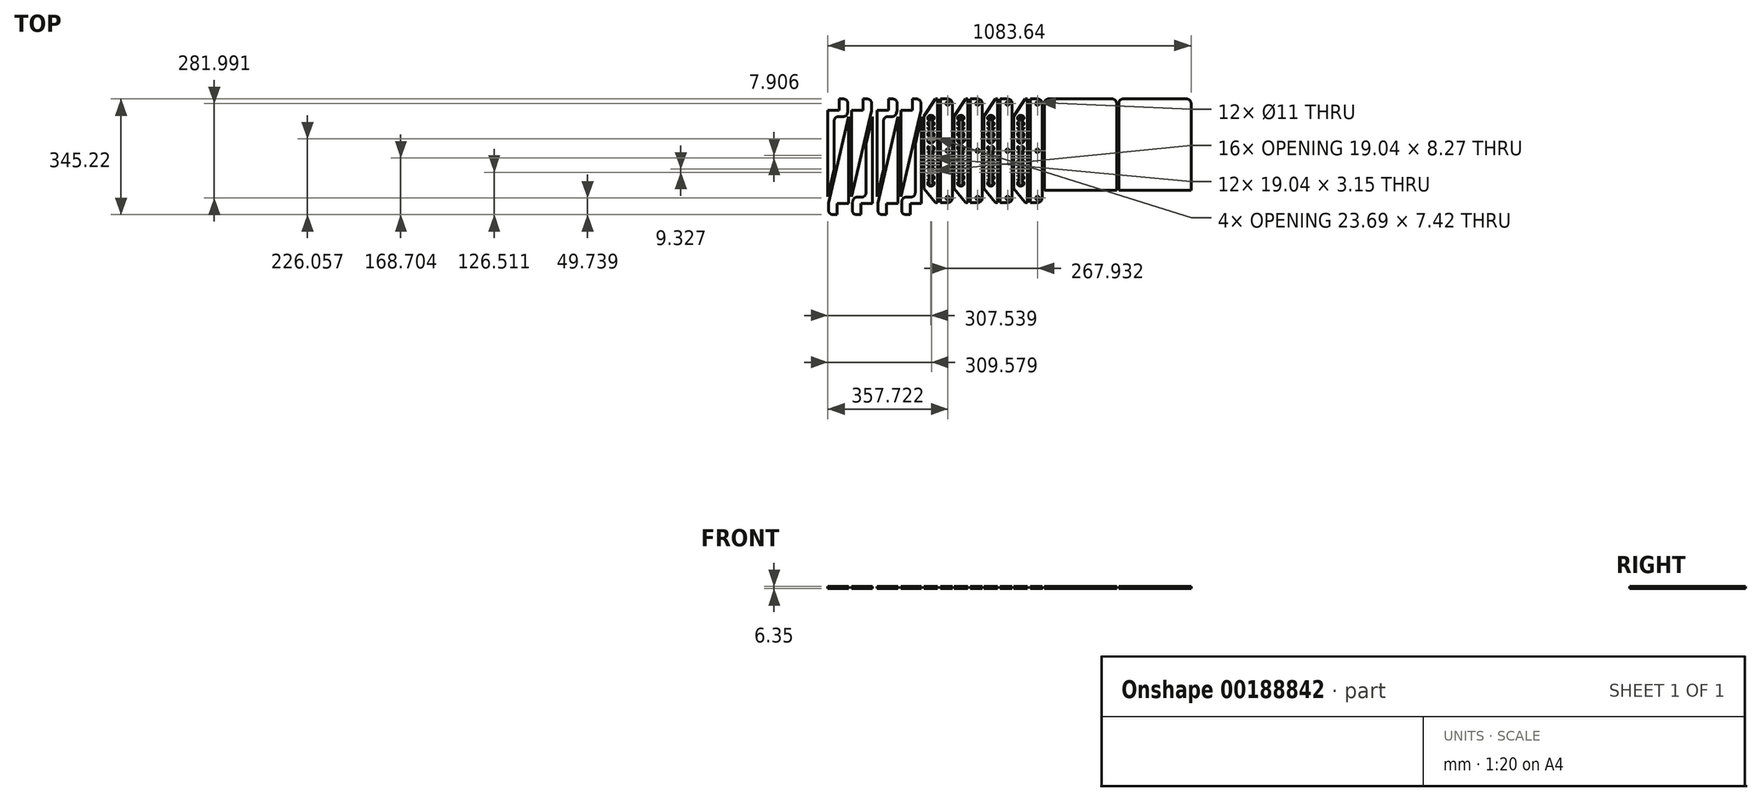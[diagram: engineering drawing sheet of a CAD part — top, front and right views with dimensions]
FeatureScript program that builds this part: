
annotation { "Feature Type Name" : "Feature", "Feature Type Description" : "" }
export const myFeature = defineFeature(function(context is Context, id is Id, definition is map)
    precondition{}
    {
        {
            var Q0;
            Q0=qCreatedBy(makeId("Top.planeOp"),FACE);
            var sketch = newSketch(context, id + "F0", { "sketchPlane" : qUnion([Q0])});
            skLineSegment(sketch, "E0.bottom", {"start": v(-174.96, 148.75) * mm, "end": v(40.94, 148.75) * mm});
            skLineSegment(sketch, "E0.top", {"start": v(-162.26, 421.8) * mm, "end": v(28.24, 421.8) * mm});
            skLineSegment(sketch, "E0.left", {"start": v(-174.96, 148.75) * mm, "end": v(-174.96, 409.1) * mm});
            skLineSegment(sketch, "E0.right", {"start": v(40.94, 148.75) * mm, "end": v(40.94, 409.1) * mm});
            skPoint(sketch, "E1.visualSharp", {"position": v(-174.96, 421.8) * mm});
            skArc(sketch, "E1.filletArc", {"start": v(-162.26, 421.8) * mm, "mid": v(-171.24, 418.08) * mm, "end": v(-174.96, 409.1) * mm});
            skPoint(sketch, "E2.visualSharp", {"position": v(40.94, 421.8) * mm});
            skArc(sketch, "E2.filletArc", {"start": v(40.94, 409.1) * mm, "mid": v(37.22, 418.08) * mm, "end": v(28.24, 421.8) * mm});
            skPoint(sketch, "E3", {"position": v(-194.8, 408.31) * mm});
            skPoint(sketch, "E4", {"position": v(-194.8, 267.31) * mm});
            skPoint(sketch, "E5", {"position": v(-194.8, 126.32) * mm});
            skLineSegment(sketch, "E6", {"start": v(-181.3, 125.53) * mm, "end": v(-181.3, 409.1) * mm});
            skLineSegment(sketch, "E7", {"start": v(-194, 112.83) * mm, "end": v(-216.87, 112.83) * mm});
            skLineSegment(sketch, "E8", {"start": v(-194, 421.8) * mm, "end": v(-216.87, 421.8) * mm});
            skPoint(sketch, "E9.visualSharp", {"position": v(-181.3, 112.83) * mm});
            skArc(sketch, "E9.filletArc", {"start": v(-194, 112.83) * mm, "mid": v(-185.03, 116.55) * mm, "end": v(-181.3, 125.53) * mm});
            skPoint(sketch, "E10.visualSharp", {"position": v(-181.3, 421.8) * mm});
            skArc(sketch, "E10.filletArc", {"start": v(-181.3, 409.1) * mm, "mid": v(-185.03, 418.08) * mm, "end": v(-194, 421.8) * mm});
            skLineSegment(sketch, "E11", {"start": v(-216.87, 112.83) * mm, "end": v(-216.87, 421.8) * mm});
            skLineSegment(sketch, "E12", {"start": v(-265.3, 154.26) * mm, "end": v(-265.3, 370.21) * mm});
            skLineSegment(sketch, "E13", {"start": v(-265.3, 370.21) * mm, "end": v(-231.01, 421.8) * mm});
            skLineSegment(sketch, "E14", {"start": v(-231.01, 421.8) * mm, "end": v(-224.66, 421.8) * mm});
            skLineSegment(sketch, "E15", {"start": v(-224.66, 421.8) * mm, "end": v(-224.66, 112.83) * mm});
            skLineSegment(sketch, "E16", {"start": v(-224.66, 112.83) * mm, "end": v(-231.01, 112.83) * mm});
            skLineSegment(sketch, "E17", {"start": v(-231.01, 112.83) * mm, "end": v(-265.3, 154.26) * mm});
            skText(sketch, "E18", { "text": "CUMMINS QSK60", "fontName": "AllertaStencil-Regular.ttf"});
            skLineSegment(sketch, "E19", {"start": v(-749.65, 129.9) * mm, "end": v(-690.3, 387.04) * mm});
            skLineSegment(sketch, "E20", {"start": v(-689.96, 389.9) * mm, "end": v(-689.96, 409.1) * mm});
            skLineSegment(sketch, "E21", {"start": v(-702.66, 421.8) * mm, "end": v(-715.36, 421.8) * mm});
            skLineSegment(sketch, "E22", {"start": v(-715.36, 421.8) * mm, "end": v(-715.36, 388.45) * mm});
            skLineSegment(sketch, "E23", {"start": v(-715.36, 388.45) * mm, "end": v(-749.65, 388.45) * mm});
            skLineSegment(sketch, "E24", {"start": v(-749.65, 388.45) * mm, "end": v(-749.65, 129.9) * mm});
            skPoint(sketch, "E25.visualSharp", {"position": v(-689.96, 421.8) * mm});
            skArc(sketch, "E25.filletArc", {"start": v(-689.96, 409.1) * mm, "mid": v(-693.68, 418.08) * mm, "end": v(-702.66, 421.8) * mm});
            skLineSegment(sketch, "E26", {"start": v(-760.76, 385.28) * mm, "end": v(-760.76, 409.1) * mm});
            skLineSegment(sketch, "E27", {"start": v(-773.46, 421.8) * mm, "end": v(-786.16, 421.8) * mm});
            skLineSegment(sketch, "E28", {"start": v(-786.16, 421.8) * mm, "end": v(-786.16, 388.45) * mm});
            skLineSegment(sketch, "E29", {"start": v(-786.16, 388.45) * mm, "end": v(-820.45, 388.45) * mm});
            skLineSegment(sketch, "E30", {"start": v(-820.45, 388.45) * mm, "end": v(-820.45, 129.9) * mm});
            skPoint(sketch, "E31.visualSharp", {"position": v(-760.76, 421.8) * mm});
            skArc(sketch, "E31.filletArc", {"start": v(-760.76, 409.1) * mm, "mid": v(-764.48, 418.08) * mm, "end": v(-773.46, 421.8) * mm});
            skPoint(sketch, "E32.visualSharp", {"position": v(-760.76, 388.45) * mm});
            skArc(sketch, "E32.filletArc", {"start": v(-761.08, 382.42) * mm, "mid": v(-760.84, 383.84) * mm, "end": v(-760.76, 385.28) * mm});
            skPoint(sketch, "E33.visualSharp", {"position": v(-689.96, 388.45) * mm});
            skArc(sketch, "E33.filletArc", {"start": v(-690.3, 387.04) * mm, "mid": v(-690.05, 388.46) * mm, "end": v(-689.96, 389.9) * mm});
            skLineSegment(sketch, "E34", {"start": v(-801.4, 356.7) * mm, "end": v(-801.4, 213.86) * mm});
            skLineSegment(sketch, "E35", {"start": v(-788.7, 369.4) * mm, "end": v(-774.2, 369.4) * mm});
            skLineSegment(sketch, "E36", {"start": v(-820.45, 129.9) * mm, "end": v(-801.72, 211) * mm});
            skLineSegment(sketch, "E37", {"start": v(-761.82, 379.24) * mm, "end": v(-761.08, 382.42) * mm});
            skPoint(sketch, "E38.visualSharp", {"position": v(-801.4, 212.42) * mm});
            skArc(sketch, "E38.filletArc", {"start": v(-801.72, 211) * mm, "mid": v(-801.48, 212.43) * mm, "end": v(-801.4, 213.86) * mm});
            skPoint(sketch, "E39.visualSharp", {"position": v(-764.09, 369.4) * mm});
            skArc(sketch, "E39.filletArc", {"start": v(-774.2, 369.4) * mm, "mid": v(-766.29, 372.16) * mm, "end": v(-761.82, 379.24) * mm});
            skPoint(sketch, "E40.visualSharp", {"position": v(-801.4, 369.4) * mm});
            skArc(sketch, "E40.filletArc", {"start": v(-788.7, 369.4) * mm, "mid": v(-797.68, 365.68) * mm, "end": v(-801.4, 356.7) * mm});
            skCircle(sketch, "E41", {"center": v(-194.8, 126.32) * mm, "radius": 5.5 * mm});
            skCircle(sketch, "E42", {"center": v(-194.8, 267.31) * mm, "radius": 5.5 * mm});
            skCircle(sketch, "E43", {"center": v(-194.8, 408.31) * mm, "radius": 5.5 * mm});
            skLineSegment(sketch, "E44", {"start": v(-602.6, 129.9) * mm, "end": v(-543.23, 387.04) * mm});
            skLineSegment(sketch, "E45", {"start": v(-542.9, 389.9) * mm, "end": v(-542.9, 409.1) * mm});
            skLineSegment(sketch, "E46", {"start": v(-555.6, 421.8) * mm, "end": v(-568.3, 421.8) * mm});
            skLineSegment(sketch, "E47", {"start": v(-568.3, 421.8) * mm, "end": v(-568.3, 388.45) * mm});
            skLineSegment(sketch, "E48", {"start": v(-568.3, 388.45) * mm, "end": v(-602.6, 388.45) * mm});
            skLineSegment(sketch, "E49", {"start": v(-602.6, 388.45) * mm, "end": v(-602.6, 129.9) * mm});
            skPoint(sketch, "E50.visualSharp", {"position": v(-542.9, 421.8) * mm});
            skArc(sketch, "E50.filletArc", {"start": v(-542.9, 409.1) * mm, "mid": v(-546.63, 418.08) * mm, "end": v(-555.6, 421.8) * mm});
            skLineSegment(sketch, "E51", {"start": v(-613.7, 389.9) * mm, "end": v(-613.7, 409.1) * mm});
            skLineSegment(sketch, "E52", {"start": v(-626.4, 421.8) * mm, "end": v(-639.1, 421.8) * mm});
            skLineSegment(sketch, "E53", {"start": v(-639.1, 421.8) * mm, "end": v(-639.1, 388.45) * mm});
            skLineSegment(sketch, "E54", {"start": v(-639.1, 388.45) * mm, "end": v(-673.39, 388.45) * mm});
            skLineSegment(sketch, "E55", {"start": v(-673.39, 388.45) * mm, "end": v(-673.39, 129.9) * mm});
            skPoint(sketch, "E56.visualSharp", {"position": v(-613.7, 421.8) * mm});
            skArc(sketch, "E56.filletArc", {"start": v(-613.7, 409.1) * mm, "mid": v(-617.42, 418.08) * mm, "end": v(-626.4, 421.8) * mm});
            skPoint(sketch, "E57.visualSharp", {"position": v(-613.7, 388.45) * mm});
            skArc(sketch, "E57.filletArc", {"start": v(-614.03, 387.04) * mm, "mid": v(-613.78, 388.46) * mm, "end": v(-613.7, 389.9) * mm});
            skPoint(sketch, "E58.visualSharp", {"position": v(-542.9, 388.45) * mm});
            skArc(sketch, "E58.filletArc", {"start": v(-543.23, 387.04) * mm, "mid": v(-542.99, 388.46) * mm, "end": v(-542.9, 389.9) * mm});
            skLineSegment(sketch, "E59", {"start": v(-654.34, 356.7) * mm, "end": v(-654.34, 213.86) * mm});
            skLineSegment(sketch, "E60", {"start": v(-641.64, 369.4) * mm, "end": v(-628.2, 369.4) * mm});
            skLineSegment(sketch, "E61", {"start": v(-673.39, 129.9) * mm, "end": v(-654.67, 211) * mm});
            skLineSegment(sketch, "E62", {"start": v(-615.83, 379.24) * mm, "end": v(-614.03, 387.04) * mm});
            skPoint(sketch, "E63.visualSharp", {"position": v(-654.34, 212.42) * mm});
            skArc(sketch, "E63.filletArc", {"start": v(-654.67, 211) * mm, "mid": v(-654.42, 212.43) * mm, "end": v(-654.34, 213.86) * mm});
            skPoint(sketch, "E64.visualSharp", {"position": v(-618.1, 369.4) * mm});
            skArc(sketch, "E64.filletArc", {"start": v(-628.2, 369.4) * mm, "mid": v(-620.3, 372.16) * mm, "end": v(-615.83, 379.24) * mm});
            skPoint(sketch, "E65.visualSharp", {"position": v(-654.34, 369.4) * mm});
            skArc(sketch, "E65.filletArc", {"start": v(-641.64, 369.4) * mm, "mid": v(-650.62, 365.68) * mm, "end": v(-654.34, 356.7) * mm});
            skPoint(sketch, "E66", {"position": v(-284.04, 408.31) * mm});
            skPoint(sketch, "E67", {"position": v(-284.04, 267.31) * mm});
            skPoint(sketch, "E68", {"position": v(-284.04, 126.32) * mm});
            skLineSegment(sketch, "E69", {"start": v(-270.55, 125.53) * mm, "end": v(-270.55, 409.1) * mm});
            skLineSegment(sketch, "E70", {"start": v(-283.25, 112.83) * mm, "end": v(-306.1, 112.83) * mm});
            skLineSegment(sketch, "E71", {"start": v(-283.25, 421.8) * mm, "end": v(-306.1, 421.8) * mm});
            skPoint(sketch, "E72.visualSharp", {"position": v(-270.55, 112.83) * mm});
            skArc(sketch, "E72.filletArc", {"start": v(-283.25, 112.83) * mm, "mid": v(-274.27, 116.55) * mm, "end": v(-270.55, 125.53) * mm});
            skPoint(sketch, "E73.visualSharp", {"position": v(-270.55, 421.8) * mm});
            skArc(sketch, "E73.filletArc", {"start": v(-270.55, 409.1) * mm, "mid": v(-274.27, 418.08) * mm, "end": v(-283.25, 421.8) * mm});
            skLineSegment(sketch, "E74", {"start": v(-306.1, 112.83) * mm, "end": v(-306.1, 421.8) * mm});
            skLineSegment(sketch, "E75", {"start": v(-354.54, 154.26) * mm, "end": v(-354.54, 370.21) * mm});
            skLineSegment(sketch, "E76", {"start": v(-354.54, 370.21) * mm, "end": v(-320.25, 421.8) * mm});
            skLineSegment(sketch, "E77", {"start": v(-320.25, 421.8) * mm, "end": v(-313.9, 421.8) * mm});
            skLineSegment(sketch, "E78", {"start": v(-313.9, 421.8) * mm, "end": v(-313.9, 112.83) * mm});
            skLineSegment(sketch, "E79", {"start": v(-313.9, 112.83) * mm, "end": v(-320.25, 112.83) * mm});
            skLineSegment(sketch, "E80", {"start": v(-320.25, 112.83) * mm, "end": v(-354.54, 154.26) * mm});
            skText(sketch, "E81", { "text": "CUMMINS QSK60", "fontName": "AllertaStencil-Regular.ttf"});
            skCircle(sketch, "E82", {"center": v(-284.04, 126.32) * mm, "radius": 5.5 * mm});
            skCircle(sketch, "E83", {"center": v(-284.04, 267.31) * mm, "radius": 5.5 * mm});
            skCircle(sketch, "E84", {"center": v(-284.04, 408.31) * mm, "radius": 5.5 * mm});
            skPoint(sketch, "E85", {"position": v(-373.49, 408.31) * mm});
            skPoint(sketch, "E86", {"position": v(-373.49, 267.31) * mm});
            skPoint(sketch, "E87", {"position": v(-373.49, 126.32) * mm});
            skLineSegment(sketch, "E88", {"start": v(-360, 125.53) * mm, "end": v(-360, 409.1) * mm});
            skLineSegment(sketch, "E89", {"start": v(-372.7, 112.83) * mm, "end": v(-395.56, 112.83) * mm});
            skLineSegment(sketch, "E90", {"start": v(-372.7, 421.8) * mm, "end": v(-395.56, 421.8) * mm});
            skPoint(sketch, "E91.visualSharp", {"position": v(-360, 112.83) * mm});
            skArc(sketch, "E91.filletArc", {"start": v(-372.7, 112.83) * mm, "mid": v(-363.72, 116.55) * mm, "end": v(-360, 125.53) * mm});
            skPoint(sketch, "E92.visualSharp", {"position": v(-360, 421.8) * mm});
            skArc(sketch, "E92.filletArc", {"start": v(-360, 409.1) * mm, "mid": v(-363.72, 418.08) * mm, "end": v(-372.7, 421.8) * mm});
            skLineSegment(sketch, "E93", {"start": v(-395.56, 112.83) * mm, "end": v(-395.56, 421.8) * mm});
            skLineSegment(sketch, "E94", {"start": v(-444, 154.26) * mm, "end": v(-444, 370.21) * mm});
            skLineSegment(sketch, "E95", {"start": v(-444, 370.21) * mm, "end": v(-409.7, 421.8) * mm});
            skLineSegment(sketch, "E96", {"start": v(-409.7, 421.8) * mm, "end": v(-403.35, 421.8) * mm});
            skLineSegment(sketch, "E97", {"start": v(-403.35, 421.8) * mm, "end": v(-403.35, 112.83) * mm});
            skLineSegment(sketch, "E98", {"start": v(-403.35, 112.83) * mm, "end": v(-409.7, 112.83) * mm});
            skLineSegment(sketch, "E99", {"start": v(-409.7, 112.83) * mm, "end": v(-444, 154.26) * mm});
            skText(sketch, "E100", { "text": "CUMMINS QSK60", "fontName": "AllertaStencil-Regular.ttf"});
            skCircle(sketch, "E101", {"center": v(-373.49, 126.32) * mm, "radius": 5.5 * mm});
            skCircle(sketch, "E102", {"center": v(-373.49, 267.31) * mm, "radius": 5.5 * mm});
            skCircle(sketch, "E103", {"center": v(-373.49, 408.31) * mm, "radius": 5.5 * mm});
            skPoint(sketch, "E104", {"position": v(-462.73, 408.31) * mm});
            skPoint(sketch, "E105", {"position": v(-462.73, 267.31) * mm});
            skPoint(sketch, "E106", {"position": v(-462.73, 126.32) * mm});
            skLineSegment(sketch, "E107", {"start": v(-449.24, 125.53) * mm, "end": v(-449.24, 409.1) * mm});
            skLineSegment(sketch, "E108", {"start": v(-461.94, 112.83) * mm, "end": v(-484.8, 112.83) * mm});
            skLineSegment(sketch, "E109", {"start": v(-461.94, 421.8) * mm, "end": v(-484.8, 421.8) * mm});
            skPoint(sketch, "E110.visualSharp", {"position": v(-449.24, 112.83) * mm});
            skArc(sketch, "E110.filletArc", {"start": v(-461.94, 112.83) * mm, "mid": v(-452.96, 116.55) * mm, "end": v(-449.24, 125.53) * mm});
            skPoint(sketch, "E111.visualSharp", {"position": v(-449.24, 421.8) * mm});
            skArc(sketch, "E111.filletArc", {"start": v(-449.24, 409.1) * mm, "mid": v(-452.96, 418.08) * mm, "end": v(-461.94, 421.8) * mm});
            skLineSegment(sketch, "E112", {"start": v(-484.8, 112.83) * mm, "end": v(-484.8, 421.8) * mm});
            skLineSegment(sketch, "E113", {"start": v(-533.23, 154.26) * mm, "end": v(-533.23, 370.21) * mm});
            skLineSegment(sketch, "E114", {"start": v(-533.23, 370.21) * mm, "end": v(-498.94, 421.8) * mm});
            skLineSegment(sketch, "E115", {"start": v(-498.94, 421.8) * mm, "end": v(-492.6, 421.8) * mm});
            skLineSegment(sketch, "E116", {"start": v(-492.6, 421.8) * mm, "end": v(-492.6, 112.83) * mm});
            skLineSegment(sketch, "E117", {"start": v(-492.6, 112.83) * mm, "end": v(-498.94, 112.83) * mm});
            skLineSegment(sketch, "E118", {"start": v(-498.94, 112.83) * mm, "end": v(-533.23, 154.26) * mm});
            skText(sketch, "E119", { "text": "CUMMINS QSK60", "fontName": "AllertaStencil-Regular.ttf"});
            skCircle(sketch, "E120", {"center": v(-462.73, 126.32) * mm, "radius": 5.5 * mm});
            skCircle(sketch, "E121", {"center": v(-462.73, 267.31) * mm, "radius": 5.5 * mm});
            skCircle(sketch, "E122", {"center": v(-462.73, 408.31) * mm, "radius": 5.5 * mm});
            skLineSegment(sketch, "E123.bottom", {"start": v(47.3, 148.75) * mm, "end": v(263.2, 148.75) * mm});
            skLineSegment(sketch, "E123.top", {"start": v(60, 421.8) * mm, "end": v(250.5, 421.8) * mm});
            skLineSegment(sketch, "E123.left", {"start": v(47.3, 148.75) * mm, "end": v(47.3, 409.1) * mm});
            skLineSegment(sketch, "E123.right", {"start": v(263.2, 148.75) * mm, "end": v(263.2, 409.1) * mm});
            skPoint(sketch, "E124.visualSharp", {"position": v(47.3, 421.8) * mm});
            skArc(sketch, "E124.filletArc", {"start": v(60, 421.8) * mm, "mid": v(51.01, 418.08) * mm, "end": v(47.3, 409.1) * mm});
            skPoint(sketch, "E125.visualSharp", {"position": v(263.2, 421.8) * mm});
            skArc(sketch, "E125.filletArc", {"start": v(263.2, 409.1) * mm, "mid": v(259.47, 418.08) * mm, "end": v(250.5, 421.8) * mm});
            skLineSegment(sketch, "E126", {"start": v(-611.51, 368.48) * mm, "end": v(-670.88, 111.34) * mm});
            skLineSegment(sketch, "E127", {"start": v(-671.2, 108.49) * mm, "end": v(-671.2, 89.28) * mm});
            skLineSegment(sketch, "E128", {"start": v(-658.5, 76.58) * mm, "end": v(-645.8, 76.58) * mm});
            skLineSegment(sketch, "E129", {"start": v(-645.8, 76.58) * mm, "end": v(-645.8, 109.93) * mm});
            skLineSegment(sketch, "E130", {"start": v(-645.8, 109.93) * mm, "end": v(-611.51, 109.93) * mm});
            skLineSegment(sketch, "E131", {"start": v(-611.51, 109.93) * mm, "end": v(-611.51, 368.48) * mm});
            skPoint(sketch, "E132.visualSharp", {"position": v(-671.2, 76.58) * mm});
            skArc(sketch, "E132.filletArc", {"start": v(-671.2, 89.28) * mm, "mid": v(-667.48, 80.3) * mm, "end": v(-658.5, 76.58) * mm});
            skLineSegment(sketch, "E133", {"start": v(-600.41, 113.1) * mm, "end": v(-600.41, 89.28) * mm});
            skLineSegment(sketch, "E134", {"start": v(-587.71, 76.58) * mm, "end": v(-575.01, 76.58) * mm});
            skLineSegment(sketch, "E135", {"start": v(-575.01, 76.58) * mm, "end": v(-575.01, 109.93) * mm});
            skLineSegment(sketch, "E136", {"start": v(-575.01, 109.93) * mm, "end": v(-540.72, 109.93) * mm});
            skLineSegment(sketch, "E137", {"start": v(-540.72, 109.93) * mm, "end": v(-540.72, 368.48) * mm});
            skPoint(sketch, "E138.visualSharp", {"position": v(-600.41, 76.58) * mm});
            skArc(sketch, "E138.filletArc", {"start": v(-600.41, 89.28) * mm, "mid": v(-596.7, 80.3) * mm, "end": v(-587.71, 76.58) * mm});
            skPoint(sketch, "E139.visualSharp", {"position": v(-600.41, 109.93) * mm});
            skArc(sketch, "E139.filletArc", {"start": v(-600.09, 115.96) * mm, "mid": v(-600.33, 114.54) * mm, "end": v(-600.41, 113.1) * mm});
            skPoint(sketch, "E140.visualSharp", {"position": v(-671.2, 109.93) * mm});
            skArc(sketch, "E140.filletArc", {"start": v(-670.88, 111.34) * mm, "mid": v(-671.12, 109.92) * mm, "end": v(-671.2, 108.49) * mm});
            skLineSegment(sketch, "E141", {"start": v(-559.77, 141.68) * mm, "end": v(-559.77, 284.52) * mm});
            skLineSegment(sketch, "E142", {"start": v(-572.47, 128.98) * mm, "end": v(-586.98, 128.98) * mm});
            skLineSegment(sketch, "E143", {"start": v(-540.72, 368.48) * mm, "end": v(-559.45, 287.37) * mm});
            skLineSegment(sketch, "E144", {"start": v(-599.35, 119.14) * mm, "end": v(-600.09, 115.96) * mm});
            skPoint(sketch, "E145.visualSharp", {"position": v(-559.77, 285.96) * mm});
            skArc(sketch, "E145.filletArc", {"start": v(-559.45, 287.37) * mm, "mid": v(-559.69, 285.96) * mm, "end": v(-559.77, 284.52) * mm});
            skPoint(sketch, "E146.visualSharp", {"position": v(-597.08, 128.98) * mm});
            skArc(sketch, "E146.filletArc", {"start": v(-586.98, 128.98) * mm, "mid": v(-594.88, 126.22) * mm, "end": v(-599.35, 119.14) * mm});
            skPoint(sketch, "E147.visualSharp", {"position": v(-559.77, 128.98) * mm});
            skArc(sketch, "E147.filletArc", {"start": v(-572.47, 128.98) * mm, "mid": v(-563.5, 132.7) * mm, "end": v(-559.77, 141.68) * mm});
            skLineSegment(sketch, "E148", {"start": v(-758.57, 368.48) * mm, "end": v(-817.93, 111.34) * mm});
            skLineSegment(sketch, "E149", {"start": v(-818.26, 108.49) * mm, "end": v(-818.26, 89.28) * mm});
            skLineSegment(sketch, "E150", {"start": v(-805.56, 76.58) * mm, "end": v(-792.86, 76.58) * mm});
            skLineSegment(sketch, "E151", {"start": v(-792.86, 76.58) * mm, "end": v(-792.86, 109.93) * mm});
            skLineSegment(sketch, "E152", {"start": v(-792.86, 109.93) * mm, "end": v(-758.57, 109.93) * mm});
            skLineSegment(sketch, "E153", {"start": v(-758.57, 109.93) * mm, "end": v(-758.57, 368.48) * mm});
            skPoint(sketch, "E154.visualSharp", {"position": v(-818.26, 76.58) * mm});
            skArc(sketch, "E154.filletArc", {"start": v(-818.26, 89.28) * mm, "mid": v(-814.54, 80.3) * mm, "end": v(-805.56, 76.58) * mm});
            skLineSegment(sketch, "E155", {"start": v(-747.47, 108.49) * mm, "end": v(-747.47, 89.28) * mm});
            skLineSegment(sketch, "E156", {"start": v(-734.77, 76.58) * mm, "end": v(-722.07, 76.58) * mm});
            skLineSegment(sketch, "E157", {"start": v(-722.07, 76.58) * mm, "end": v(-722.07, 109.93) * mm});
            skLineSegment(sketch, "E158", {"start": v(-722.07, 109.93) * mm, "end": v(-687.78, 109.93) * mm});
            skLineSegment(sketch, "E159", {"start": v(-687.78, 109.93) * mm, "end": v(-687.78, 368.48) * mm});
            skPoint(sketch, "E160.visualSharp", {"position": v(-747.47, 76.58) * mm});
            skArc(sketch, "E160.filletArc", {"start": v(-747.47, 89.28) * mm, "mid": v(-743.75, 80.3) * mm, "end": v(-734.77, 76.58) * mm});
            skPoint(sketch, "E161.visualSharp", {"position": v(-747.47, 109.93) * mm});
            skArc(sketch, "E161.filletArc", {"start": v(-747.14, 111.34) * mm, "mid": v(-747.39, 109.92) * mm, "end": v(-747.47, 108.49) * mm});
            skPoint(sketch, "E162.visualSharp", {"position": v(-818.26, 109.93) * mm});
            skArc(sketch, "E162.filletArc", {"start": v(-817.93, 111.34) * mm, "mid": v(-818.18, 109.92) * mm, "end": v(-818.26, 108.49) * mm});
            skLineSegment(sketch, "E163", {"start": v(-706.83, 141.68) * mm, "end": v(-706.83, 284.52) * mm});
            skLineSegment(sketch, "E164", {"start": v(-719.53, 128.98) * mm, "end": v(-732.97, 128.98) * mm});
            skLineSegment(sketch, "E165", {"start": v(-687.78, 368.48) * mm, "end": v(-706.5, 287.37) * mm});
            skLineSegment(sketch, "E166", {"start": v(-745.34, 119.14) * mm, "end": v(-747.14, 111.34) * mm});
            skPoint(sketch, "E167.visualSharp", {"position": v(-706.83, 285.96) * mm});
            skArc(sketch, "E167.filletArc", {"start": v(-706.5, 287.37) * mm, "mid": v(-706.75, 285.96) * mm, "end": v(-706.83, 284.52) * mm});
            skPoint(sketch, "E168.visualSharp", {"position": v(-743.07, 128.98) * mm});
            skArc(sketch, "E168.filletArc", {"start": v(-732.97, 128.98) * mm, "mid": v(-740.87, 126.22) * mm, "end": v(-745.34, 119.14) * mm});
            skPoint(sketch, "E169.visualSharp", {"position": v(-706.83, 128.98) * mm});
            skArc(sketch, "E169.filletArc", {"start": v(-719.53, 128.98) * mm, "mid": v(-710.55, 132.7) * mm, "end": v(-706.83, 141.68) * mm});
            skLineSegment(sketch, "E170", {"start": v(316.79, 421.8) * mm, "end": v(-842.8, 421.8) * mm, "construction": true});
            const initialGuessF0  = {"E18": [-0.23546, 0.1602, 0, 1, 0.01905], "E81": [-0.3247, 0.1602, 0, 1, 0.01905], "E100": [-0.41415, 0.1602, 0, 1, 0.01905], "E119": [-0.50339, 0.1602, 0, 1, 0.01905]};
            skSetInitialGuess(sketch, initialGuessF0);
            skSolve(sketch);
        }
        {
            var Q0;
            Q0=makeQuery(id+"F0.imprint","IMPRINT",FACE,{"disambiguationData":[TD([[makeQuery(id+"F0.imprint","IMPRINT",EDGE,{"derivedFrom":sQuery(id+"F0.wireOp",EDGE,"E107")}),1.0]])]});
            var Q1;
            Q1=makeQuery(id+"F0.imprint","IMPRINT",FACE,{"disambiguationData":[TD([[makeQuery(id+"F0.imprint","IMPRINT",EDGE,{"derivedFrom":sQuery(id+"F0.wireOp",EDGE,"E113")}),-1.0]])]});
            var Q2;
            Q2=makeQuery(id+"F0.imprint","IMPRINT",FACE,{"disambiguationData":[TD([[makeQuery(id+"F0.imprint","IMPRINT",EDGE,{"derivedFrom":sQuery(id+"F0.wireOp",EDGE,"E133")}),1.0]])]});
            var Q3;
            Q3=makeQuery(id+"F0.imprint","IMPRINT",FACE,{"disambiguationData":[TD([[makeQuery(id+"F0.imprint","IMPRINT",EDGE,{"derivedFrom":sQuery(id+"F0.wireOp",EDGE,"E44")}),1.0]])]});
            var Q4;
            Q4=makeQuery(id+"F0.imprint","IMPRINT",FACE,{"disambiguationData":[TD([[makeQuery(id+"F0.imprint","IMPRINT",EDGE,{"derivedFrom":sQuery(id+"F0.wireOp",EDGE,"E126")}),1.0]])]});
            var Q5;
            Q5=makeQuery(id+"F0.imprint","IMPRINT",FACE,{"disambiguationData":[TD([[makeQuery(id+"F0.imprint","IMPRINT",EDGE,{"derivedFrom":sQuery(id+"F0.wireOp",EDGE,"E51")}),1.0]])]});
            var Q6;
            Q6=makeQuery(id+"F0.imprint","IMPRINT",FACE,{"disambiguationData":[TD([[makeQuery(id+"F0.imprint","IMPRINT",EDGE,{"derivedFrom":sQuery(id+"F0.wireOp",EDGE,"E155")}),1.0]])]});
            var Q7;
            Q7=makeQuery(id+"F0.imprint","IMPRINT",FACE,{"disambiguationData":[TD([[makeQuery(id+"F0.imprint","IMPRINT",EDGE,{"derivedFrom":sQuery(id+"F0.wireOp",EDGE,"E19")}),1.0]])]});
            var Q8;
            Q8=makeQuery(id+"F0.imprint","IMPRINT",FACE,{"disambiguationData":[TD([[makeQuery(id+"F0.imprint","IMPRINT",EDGE,{"derivedFrom":sQuery(id+"F0.wireOp",EDGE,"E148")}),1.0]])]});
            var Q9;
            Q9=makeQuery(id+"F0.imprint","IMPRINT",FACE,{"disambiguationData":[TD([[makeQuery(id+"F0.imprint","IMPRINT",EDGE,{"derivedFrom":sQuery(id+"F0.wireOp",EDGE,"E26")}),1.0]])]});
            extrude(context, id + "F1", {"entities" : qUnion([Q0, Q1, Q2, Q3, Q4, Q5, Q6, Q7, Q8, Q9]), "depth" : 6.35 * mm});
        }
        {
            var Q0;
            Q0=makeQuery(id+"F0.imprint","IMPRINT",FACE,{"disambiguationData":[TD([[makeQuery(id+"F0.imprint","IMPRINT",EDGE,{"derivedFrom":sQuery(id+"F0.wireOp",EDGE,"E94")}),-1.0]])]});
            var Q1;
            Q1=makeQuery(id+"F0.imprint","IMPRINT",FACE,{"disambiguationData":[TD([[makeQuery(id+"F0.imprint","IMPRINT",EDGE,{"derivedFrom":sQuery(id+"F0.wireOp",EDGE,"E88")}),1.0]])]});
            var Q2;
            Q2=makeQuery(id+"F0.imprint","IMPRINT",FACE,{"disambiguationData":[TD([[makeQuery(id+"F0.imprint","IMPRINT",EDGE,{"derivedFrom":sQuery(id+"F0.wireOp",EDGE,"E75")}),-1.0]])]});
            var Q3;
            Q3=makeQuery(id+"F0.imprint","IMPRINT",FACE,{"disambiguationData":[TD([[makeQuery(id+"F0.imprint","IMPRINT",EDGE,{"derivedFrom":sQuery(id+"F0.wireOp",EDGE,"E69")}),1.0]])]});
            var Q4;
            Q4=makeQuery(id+"F0.imprint","IMPRINT",FACE,{"disambiguationData":[TD([[makeQuery(id+"F0.imprint","IMPRINT",EDGE,{"derivedFrom":sQuery(id+"F0.wireOp",EDGE,"E12")}),-1.0]])]});
            var Q5;
            Q5=makeQuery(id+"F0.imprint","IMPRINT",FACE,{"disambiguationData":[TD([[makeQuery(id+"F0.imprint","IMPRINT",EDGE,{"derivedFrom":sQuery(id+"F0.wireOp",EDGE,"E6")}),1.0]])]});
            var Q6;
            Q6=makeQuery(id+"F0.imprint","IMPRINT",FACE,{"disambiguationData":[TD([[makeQuery(id+"F0.imprint","IMPRINT",EDGE,{"derivedFrom":sQuery(id+"F0.wireOp",EDGE,"E0.bottom")}),1.0]])]});
            var Q7;
            Q7=makeQuery(id+"F0.imprint","IMPRINT",FACE,{"disambiguationData":[TD([[makeQuery(id+"F0.imprint","IMPRINT",EDGE,{"derivedFrom":sQuery(id+"F0.wireOp",EDGE,"E123.bottom")}),1.0]])]});
            extrude(context, id + "F2", {"entities" : qUnion([Q0, Q1, Q2, Q3, Q4, Q5, Q6, Q7]), "depth" : 6.35 * mm});
        }
    });
